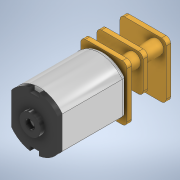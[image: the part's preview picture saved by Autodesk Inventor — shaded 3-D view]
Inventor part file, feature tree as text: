
AUTODESK INVENTOR PART (.ipt)
format: ipt  version: 2022 (Build 260153000, 153)  size: 314,880 bytes
history: native  units: mm
features: extrude x10, sketch x10, projected_geometry x3, fillet x1
ambient origin geometry x8: Origin, YZ Plane, XZ Plane, XY Plane, X Axis, Y Axis, Z Axis, Center Point
bodies: 实体1 (feature_tree), 实体2 (feature_tree), 实体3 (feature_tree)
feature tree (24):
  extrude  "拉伸1"  Depth=2.0mm
  extrude  "拉伸2"  Depth=10.0mm
  extrude  "拉伸3"  Depth=6.0mm
  fillet  "圆角1"  Radius=1.0mm
  extrude  "拉伸4"  Depth=1.0mm TaperAngle=0.0deg
  extrude  "拉伸5"  Depth=1.0mm
  extrude  "拉伸6"  Depth=10.0mm
  extrude  "拉伸7"  Depth=1.0mm TaperAngle=0.0deg
  extrude  "拉伸8"  Depth=2.0mm
  extrude  "拉伸9"  Depth=2.0mm
  extrude  "拉伸12"  Depth=1.0mm TaperAngle=0.0deg
  sketch  "草图1"  dims[d0=4.5mm d1=2.0mm]
  sketch  "草图2"  dims[d2=1.0mm d3=0.0mm d4=10.0mm]
  sketch  "草图3"  dims[d7=7.0mm d8=6.0mm d9=1.0mm]
  projected_geometry  "投影回路1"
  sketch  "草图4"  dims[d10=2.0mm d11=1.0mm d12=0.0mm]
  sketch  "草图5"  dims[d13=14.0mm d14=0.0mm d15=1.0mm]
  sketch  "草图6"  dims[d16=1.0mm d17=10.0mm]
  projected_geometry  "投影回路2"
  sketch  "草图7"  dims[d18=12.0mm d19=1.0mm d20=0.0mm]
  sketch  "草图8"  dims[d21=3.0mm d22=2.0mm]
  projected_geometry  "投影回路3"
  sketch  "草图9"  dims[d23=2.0mm d24=2.0mm]
  sketch  "草图11"  dims[d25=2.0mm d26=2.5mm d27=0.0mm d28=1.0mm d29=0.0mm d30=4.0mm d31=0.0mm d32=1.0mm d33=0.0mm d34=4.0mm d35=3.0mm d36=0.5mm d37=0.0mm d45=4.0mm d46=1.0mm d47=1.0mm d48=1.5mm d49=0.0mm]
